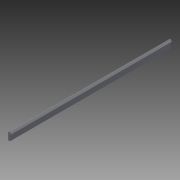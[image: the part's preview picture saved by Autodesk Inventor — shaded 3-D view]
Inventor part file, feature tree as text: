
AUTODESK INVENTOR PART (.ipt)
format: ipt  version: 2016 SP1 (Build 200210100, 210)  size: 99,840 bytes
history: native  units: in
note: dims shown in document units (in); Inventor stores cm internally (conversion verified against a paired STEP export)
features: fillet x1, other x1, imported_body x1
ambient origin geometry x8: Origin, YZ Plane, XZ Plane, XY Plane, X Axis, Y Axis, Z Axis, Center Point
bodies: Body1 (feature_tree)
feature tree (3):
  fillet  "Fillet1"  [1 undecoded]
  other  "BWC-T2-11"
  imported_body  "Base1"
note: 1 required parameter value undecoded (feature->parameter linkage not recoverable at this tier; creation-order binding heuristic only, values carry confidence <= 0.55)
